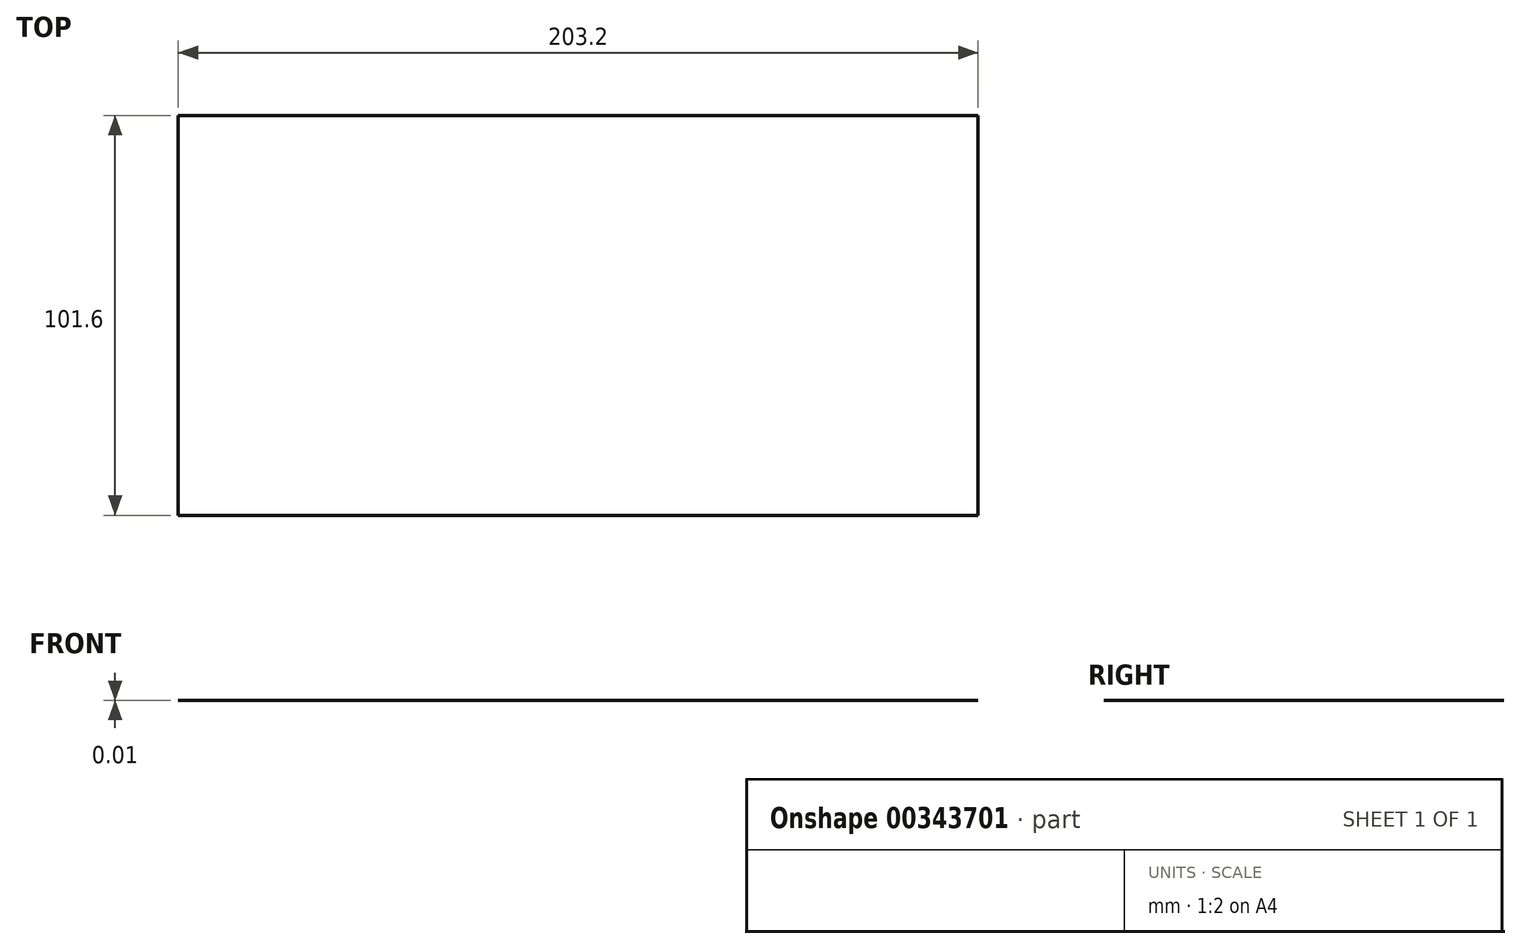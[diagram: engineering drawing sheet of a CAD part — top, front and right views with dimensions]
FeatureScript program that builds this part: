
annotation { "Feature Type Name" : "Feature", "Feature Type Description" : "" }
export const myFeature = defineFeature(function(context is Context, id is Id, definition is map)
    precondition{}
    {
        {
            var Q0;
            Q0=qCreatedBy(makeId("Top.planeOp"),FACE);
            var sketch = newSketch(context, id + "F0", { "sketchPlane" : qUnion([Q0])});
            skLineSegment(sketch, "E0.bottom", {"start": v(0, 0) * mm, "end": v(-120, 0) * mm});
            skLineSegment(sketch, "E0.top", {"start": v(0, 52) * mm, "end": v(-120, 52) * mm});
            skLineSegment(sketch, "E0.left", {"start": v(0, 0) * mm, "end": v(0, 52) * mm});
            skLineSegment(sketch, "E0.right", {"start": v(-120, 0) * mm, "end": v(-120, 52) * mm});
            skLineSegment(sketch, "E1", {"start": v(-120, 6) * mm, "end": v(0, 6) * mm});
            skLineSegment(sketch, "E2", {"start": v(-9.5, 0) * mm, "end": v(-9.5, 52) * mm});
            skLineSegment(sketch, "E3", {"start": v(-76.5, 0) * mm, "end": v(-76.5, 52) * mm});
            skPoint(sketch, "E4", {"position": v(-76.5, 6) * mm});
            skPoint(sketch, "E5", {"position": v(-9.5, 6) * mm});
            skSolve(sketch);
        }
        {
            var Q0;
            Q0=qCreatedBy(makeId("Top.planeOp"),FACE);
            var sketch = newSketch(context, id + "F1", { "sketchPlane" : qUnion([Q0])});
            skLineSegment(sketch, "E6.bottom", {"start": v(203.2, 0) * mm, "end": v(0, 0) * mm});
            skLineSegment(sketch, "E6.top", {"start": v(203.2, 101.6) * mm, "end": v(0, 101.6) * mm});
            skLineSegment(sketch, "E6.left", {"start": v(203.2, 0) * mm, "end": v(203.2, 101.6) * mm});
            skLineSegment(sketch, "E6.right", {"start": v(0, 0) * mm, "end": v(0, 101.6) * mm});
            skPoint(sketch, "E6.middle", {"position": v(101.6, 50.8) * mm});
            skSolve(sketch);
        }
        {
            var Q0;
            Q0=makeQuery(id+"F1.imprint","IMPRINT",FACE,{"disambiguationData":[TD([[makeQuery(id+"F1.imprint","IMPRINT",EDGE,{"derivedFrom":sQuery(id+"F1.wireOp",EDGE,"E6.bottom")}),-1.0]])]});
            extrude(context, id + "F2", {"entities" : qUnion([Q0]), "depth" : 1 / 101.6 * mm});
        }
    });
